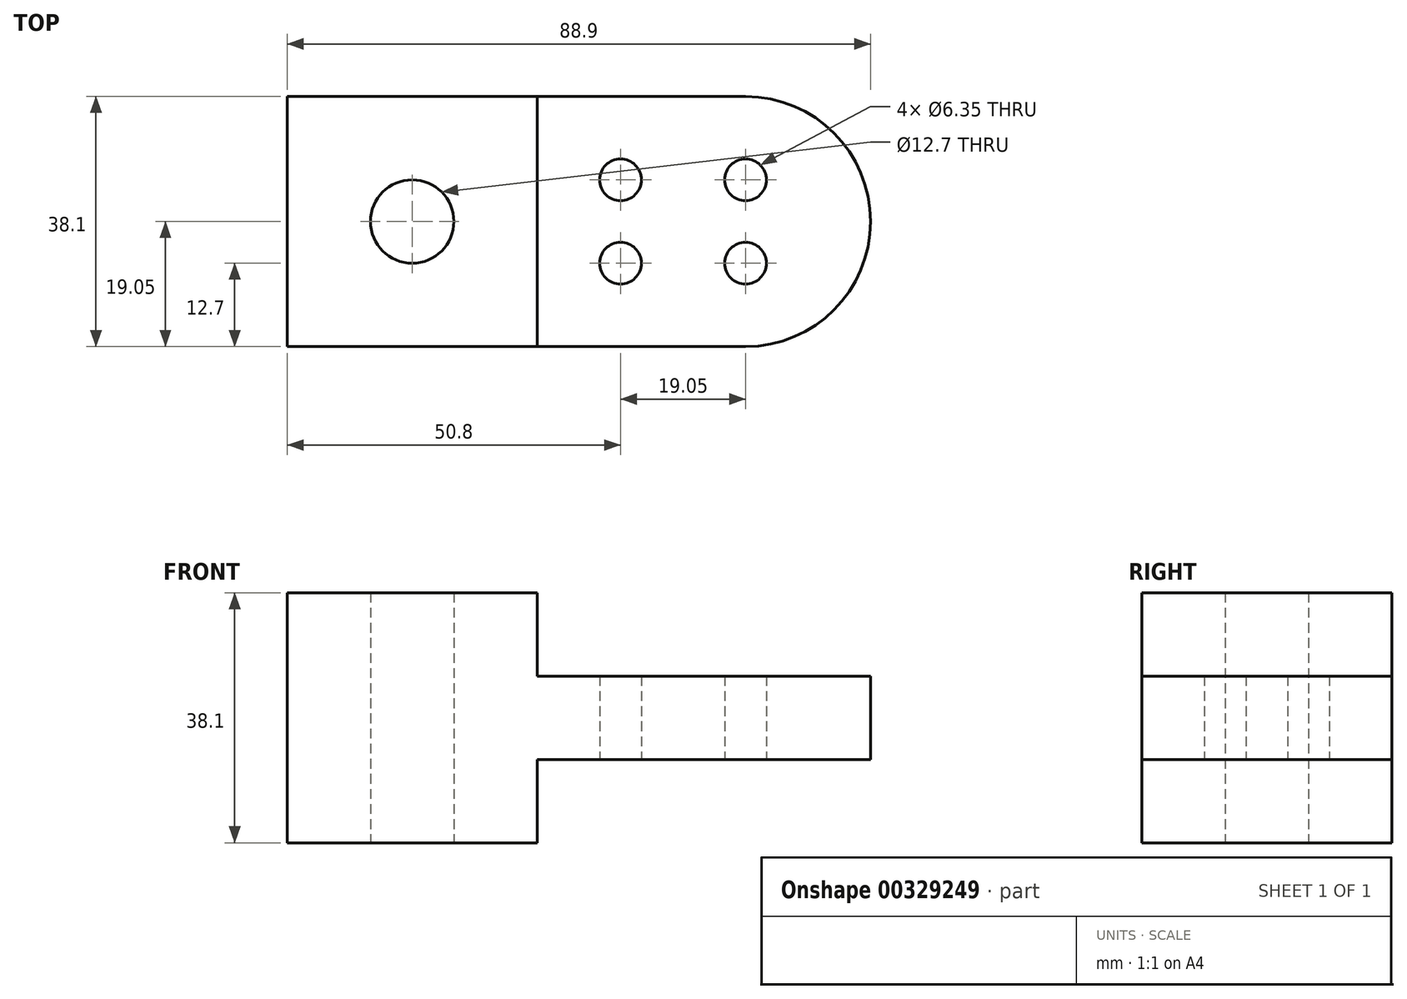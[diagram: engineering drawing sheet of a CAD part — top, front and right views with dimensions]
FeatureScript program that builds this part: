
annotation { "Feature Type Name" : "Feature", "Feature Type Description" : "" }
export const myFeature = defineFeature(function(context is Context, id is Id, definition is map)
    precondition{}
    {
        {
            var Q0;
            Q0=qCreatedBy(makeId("Top.planeOp"),FACE);
            var sketch = newSketch(context, id + "F0", { "sketchPlane" : qUnion([Q0])});
            skLineSegment(sketch, "E0", {"start": v(0, -19.05) * mm, "end": v(0, 19.05) * mm});
            skLineSegment(sketch, "E1", {"start": v(0, 19.05) * mm, "end": v(69.85, 19.05) * mm});
            skLineSegment(sketch, "E2", {"start": v(0, -19.05) * mm, "end": v(69.85, -19.05) * mm});
            skArc(sketch, "E3", {"start": v(69.85, -19.05) * mm, "mid": v(88.9, 0) * mm, "end": v(69.85, 19.05) * mm});
            skCircle(sketch, "E4", {"center": v(19.05, 0) * mm, "radius": 6.35 * mm});
            skCircle(sketch, "E5", {"center": v(50.8, 6.35) * mm, "radius": 3.18 * mm});
            skCircle(sketch, "E6", {"center": v(69.85, 6.35) * mm, "radius": 3.18 * mm});
            skCircle(sketch, "E7", {"center": v(50.8, -6.35) * mm, "radius": 3.18 * mm});
            skCircle(sketch, "E8", {"center": v(69.85, -6.35) * mm, "radius": 3.18 * mm});
            skSolve(sketch);
        }
        {
            var Q0;
            Q0=makeQuery(id+"F0.imprint","IMPRINT",FACE,{"disambiguationData":[TD([[makeQuery(id+"F0.imprint","IMPRINT",EDGE,{"derivedFrom":sQuery(id+"F0.wireOp",EDGE,"E0")}),-1.0]])]});
            extrude(context, id + "F1", {"entities" : qUnion([Q0]), "endBound" : BoundingType.SYMMETRIC, "depth" : 12.7 * mm});
        }
        {
            var Q0;
            Q0=qCreatedBy(makeId("Top.planeOp"),FACE);
            var sketch = newSketch(context, id + "F2", { "sketchPlane" : qUnion([Q0])});
            skLineSegment(sketch, "E9.bottom", {"start": v(0, 19.05) * mm, "end": v(38.1, 19.05) * mm});
            skLineSegment(sketch, "E9.top", {"start": v(0, -19.05) * mm, "end": v(38.1, -19.05) * mm});
            skLineSegment(sketch, "E9.left", {"start": v(0, 19.05) * mm, "end": v(0, -19.05) * mm});
            skLineSegment(sketch, "E9.right", {"start": v(38.1, 19.05) * mm, "end": v(38.1, -19.05) * mm});
            skCircle(sketch, "E10", {"center": v(19.05, 0) * mm, "radius": 6.35 * mm});
            skSolve(sketch);
        }
        {
            var Q0;
            Q0 = qSketchRegion(id + "F2", true);
            extrude(context, id + "F3", {"entities" : qUnion([Q0]), "operationType" : NewBodyOperationType.ADD, "endBound" : BoundingType.SYMMETRIC, "depth" : 38.1 * mm});
        }
    });
